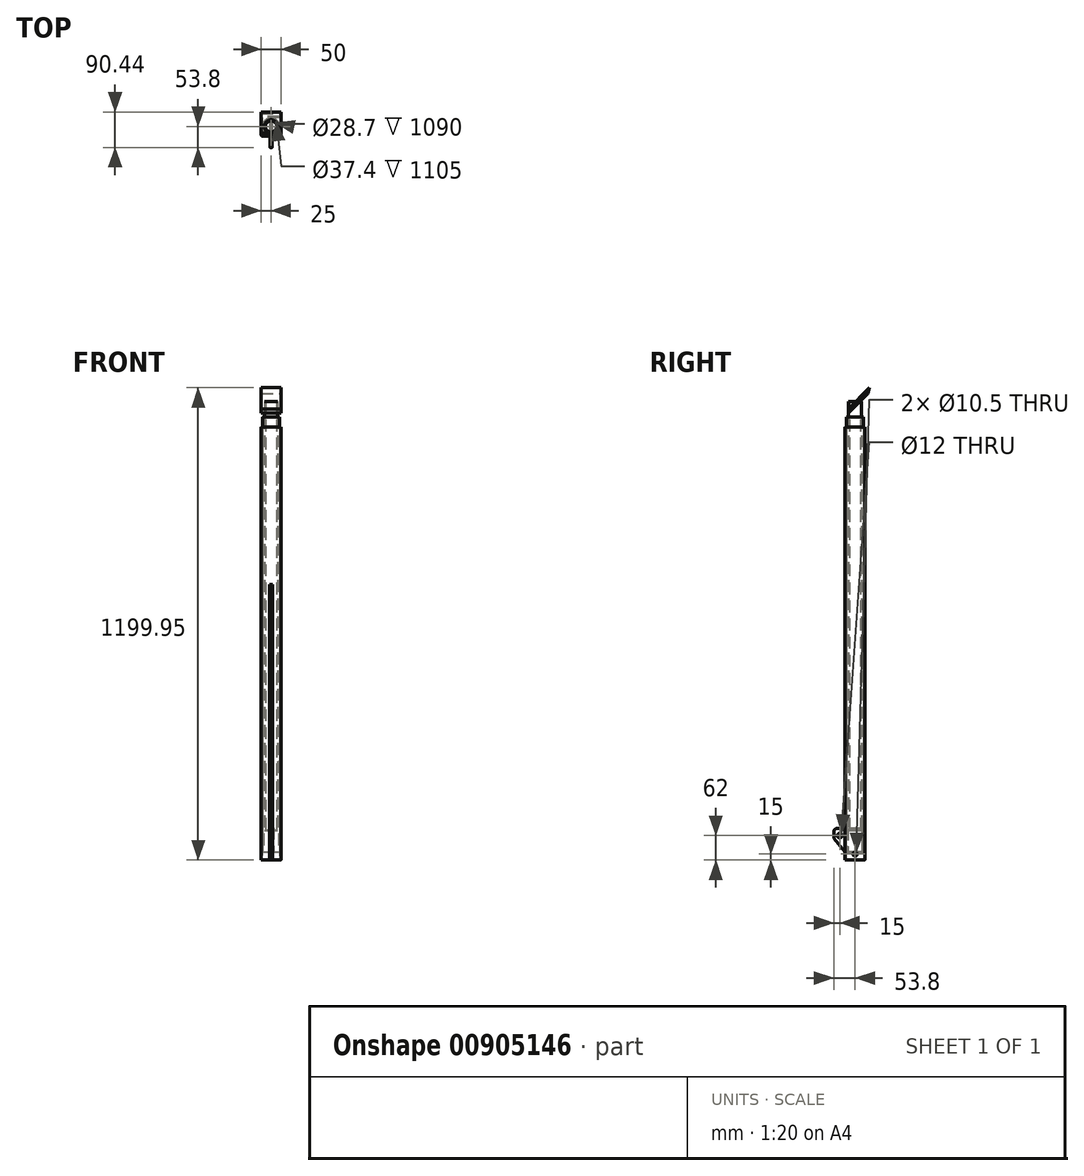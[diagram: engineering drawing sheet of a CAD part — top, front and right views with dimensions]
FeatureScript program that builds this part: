
annotation { "Feature Type Name" : "Feature", "Feature Type Description" : "" }
export const myFeature = defineFeature(function(context is Context, id is Id, definition is map)
    precondition{}
    {
        {
            var Q0;
            Q0=qCreatedBy(makeId("Top.planeOp"),FACE);
            var sketch = newSketch(context, id + "F0", { "sketchPlane" : qUnion([Q0])});
            skLineSegment(sketch, "E0.bottom", {"start": v(21, 25) * mm, "end": v(-21, 25) * mm});
            skLineSegment(sketch, "E0.top", {"start": v(21, -25) * mm, "end": v(-21, -25) * mm});
            skLineSegment(sketch, "E0.left", {"start": v(25, 21) * mm, "end": v(25, -21) * mm});
            skLineSegment(sketch, "E0.right", {"start": v(-25, 21) * mm, "end": v(-25, -21) * mm});
            skPoint(sketch, "E0.middle", {"position": v(0, 0) * mm});
            skLineSegment(sketch, "E1.bottom", {"start": v(21, 23) * mm, "end": v(-21, 23) * mm});
            skLineSegment(sketch, "E1.top", {"start": v(21, -23) * mm, "end": v(-21, -23) * mm});
            skLineSegment(sketch, "E1.left", {"start": v(23, 21) * mm, "end": v(23, -21) * mm});
            skLineSegment(sketch, "E1.right", {"start": v(-23, 21) * mm, "end": v(-23, -21) * mm});
            skPoint(sketch, "E2.visualSharp", {"position": v(-25, 25) * mm});
            skArc(sketch, "E2.filletArc", {"start": v(-21, 25) * mm, "mid": v(-23.83, 23.83) * mm, "end": v(-25, 21) * mm});
            skPoint(sketch, "E3.visualSharp", {"position": v(25, 25) * mm});
            skArc(sketch, "E3.filletArc", {"start": v(25, 21) * mm, "mid": v(23.83, 23.83) * mm, "end": v(21, 25) * mm});
            skPoint(sketch, "E4.visualSharp", {"position": v(25, -25) * mm});
            skArc(sketch, "E4.filletArc", {"start": v(21, -25) * mm, "mid": v(23.83, -23.83) * mm, "end": v(25, -21) * mm});
            skPoint(sketch, "E5.visualSharp", {"position": v(-25, -25) * mm});
            skArc(sketch, "E5.filletArc", {"start": v(-25, -21) * mm, "mid": v(-23.83, -23.83) * mm, "end": v(-21, -25) * mm});
            skPoint(sketch, "E6.visualSharp", {"position": v(23, 23) * mm});
            skArc(sketch, "E6.filletArc", {"start": v(23, 21) * mm, "mid": v(22.41, 22.41) * mm, "end": v(21, 23) * mm});
            skPoint(sketch, "E7.visualSharp", {"position": v(23, -23) * mm});
            skArc(sketch, "E7.filletArc", {"start": v(21, -23) * mm, "mid": v(22.41, -22.41) * mm, "end": v(23, -21) * mm});
            skPoint(sketch, "E8.visualSharp", {"position": v(-23, -23) * mm});
            skArc(sketch, "E8.filletArc", {"start": v(-23, -21) * mm, "mid": v(-22.41, -22.41) * mm, "end": v(-21, -23) * mm});
            skPoint(sketch, "E9.visualSharp", {"position": v(-23, 23) * mm});
            skArc(sketch, "E9.filletArc", {"start": v(-21, 23) * mm, "mid": v(-22.41, 22.41) * mm, "end": v(-23, 21) * mm});
            skSolve(sketch);
        }
        {
            var Q0;
            Q0=makeQuery(id+"F0.imprint","IMPRINT",FACE,{"disambiguationData":[TD([[makeQuery(id+"F0.imprint","IMPRINT",EDGE,{"derivedFrom":sQuery(id+"F0.wireOp",EDGE,"E0.bottom")}),1.0]])]});
            extrude(context, id + "F1", {"entities" : qUnion([Q0]), "depth" : 1100 * mm, "offsetDistance" : 25 * mm});
        }
        {
            var Q0;
            Q0=qCreatedBy(makeId("Top.planeOp"),FACE);
            var sketch = newSketch(context, id + "F2", { "sketchPlane" : qUnion([Q0])});
            skCircle(sketch, "E10", {"center": v(0, 0) * mm, "radius": 21.2 * mm});
            skCircle(sketch, "E11", {"center": v(0, 0) * mm, "radius": 18.7 * mm});
            skSolve(sketch);
        }
        {
            var Q0;
            Q0=makeQuery(id+"F2.imprint","IMPRINT",FACE,{"disambiguationData":[TD([[makeQuery(id+"F2.imprint","IMPRINT",EDGE,{"derivedFrom":sQuery(id+"F2.wireOp",EDGE,"E10")}),1.0]])]});
            extrude(context, id + "F3", {"entities" : qUnion([Q0]), "depth" : 1105 * mm, "offsetDistance" : 25 * mm});
        }
        {
            var Q0;
            Q0=qCreatedBy(makeId("Top.planeOp"),FACE);
            var sketch = newSketch(context, id + "F4", { "sketchPlane" : qUnion([Q0])});
            skCircle(sketch, "E12", {"center": v(0, 0) * mm, "radius": 16.85 * mm});
            skCircle(sketch, "E13", {"center": v(0, 0) * mm, "radius": 14.35 * mm});
            skSolve(sketch);
        }
        {
            var Q0;
            Q0=makeQuery(id+"F4.imprint","IMPRINT",FACE,{"disambiguationData":[TD([[makeQuery(id+"F4.imprint","IMPRINT",EDGE,{"derivedFrom":sQuery(id+"F4.wireOp",EDGE,"E12")}),1.0]])]});
            extrude(context, id + "F5", {"entities" : qUnion([Q0]), "depth" : 1090 * mm, "offsetDistance" : 25 * mm});
        }
        {
            var Q0;
            Q0=makeQuery(id+"F1.opExtrude","SWEPT_FACE",FACE,{"disambiguationData":[OSD([sQuery(id+"F0.wireOp",EDGE,"E0.top")])]});
            var sketch = newSketch(context, id + "F6", { "sketchPlane" : qUnion([Q0])});
            skLineSegment(sketch, "E14.bottom", {"start": v(-4, 0) * mm, "end": v(4, 0) * mm});
            skLineSegment(sketch, "E14.top", {"start": v(-4, 700) * mm, "end": v(4, 700) * mm});
            skLineSegment(sketch, "E14.left", {"start": v(-4, 0) * mm, "end": v(-4, 700) * mm});
            skLineSegment(sketch, "E14.right", {"start": v(4, 0) * mm, "end": v(4, 700) * mm});
            skSolve(sketch);
        }
        {
            var Q0;
            Q0=makeQuery(id+"F6.imprint","IMPRINT",FACE,{"disambiguationData":[TD([[makeQuery(id+"F6.imprint","IMPRINT",EDGE,{"derivedFrom":sQuery(id+"F6.wireOp",EDGE,"E14.bottom")}),-1.0]])]});
            extrude(context, id + "F7", {"entities" : qUnion([Q0]), "operationType" : NewBodyOperationType.REMOVE, "endBound" : BoundingType.UP_TO_NEXT, "oppositeDirection" : true, "depth" : 25 * mm, "offsetDistance" : 25 * mm});
        }
        {
            var Q0;
            Q0=makeQuery(id+"F3.opExtrude","SWEPT_BODY",BODY,{"disambiguationData":[OSD([sQuery(id+"F2.wireOp",EDGE,"E10"),sQuery(id+"F2.wireOp",EDGE,"E11")])]});
            var Q1;
            Q1=makeQuery(id+"F5.opExtrude","SWEPT_BODY",BODY,{"disambiguationData":[OSD([sQuery(id+"F4.wireOp",EDGE,"E12"),sQuery(id+"F4.wireOp",EDGE,"E13")])]});
            transform(context, id + "F8", {"entities" : qUnion([Q0, Q1]), "transformType" : TransformType.TRANSLATION_3D, "dx" : 0 * mm, "dy" : 0 * mm, "dz" : 25 * mm, "makeCopy" : false});
        }
        {
            var Q0;
            Q0=makeQuery(id+"F3.opExtrude","SWEPT_BODY",BODY,{"disambiguationData":[OSD([sQuery(id+"F2.wireOp",EDGE,"E10"),sQuery(id+"F2.wireOp",EDGE,"E11")])]});
            transform(context, id + "F9", {"entities" : qUnion([Q0]), "transformType" : TransformType.TRANSLATION_3D, "dx" : 0 * mm, "dy" : 0 * mm, "dz" : -25 * mm, "makeCopy" : false});
        }
        {
            var Q0;
            Q0=makeQuery(id+"F1.opExtrude","SWEPT_FACE",FACE,{"disambiguationData":[OSD([sQuery(id+"F0.wireOp",EDGE,"E0.left")])]});
            var sketch = newSketch(context, id + "F10", { "sketchPlane" : qUnion([Q0])});
            skCircle(sketch, "E15", {"center": v(0, 15) * mm, "radius": 5.25 * mm});
            skSolve(sketch);
        }
        {
            var Q0;
            Q0=makeQuery(id+"F5.opExtrude","SWEPT_BODY",BODY,{"disambiguationData":[OSD([sQuery(id+"F4.wireOp",EDGE,"E12"),sQuery(id+"F4.wireOp",EDGE,"E13")])]});
            transform(context, id + "F11", {"entities" : qUnion([Q0]), "transformType" : TransformType.TRANSLATION_3D, "dx" : 0 * mm, "dy" : 0 * mm, "dz" : 50 * mm, "makeCopy" : false});
        }
        {
            var Q0;
            Q0=qCreatedBy(makeId("Right.planeOp"),FACE);
            var sketch = newSketch(context, id + "F12", { "sketchPlane" : qUnion([Q0])});
            skLineSegment(sketch, "E16", {"start": v(21.2, 0) * mm, "end": v(21.2, 60) * mm});
            skLineSegment(sketch, "E17", {"start": v(21.2, 60) * mm, "end": v(-53.8, 60) * mm});
            skLineSegment(sketch, "E18", {"start": v(-53.8, 60) * mm, "end": v(-53.8, 35) * mm});
            skLineSegment(sketch, "E19", {"start": v(-53.8, 35) * mm, "end": v(-25, 0) * mm});
            skLineSegment(sketch, "E20", {"start": v(-25, 0) * mm, "end": v(21.2, 0) * mm});
            skSolve(sketch);
        }
        {
            var Q0;
            Q0=makeQuery(id+"F12.imprint","IMPRINT",FACE,{"disambiguationData":[TD([[makeQuery(id+"F12.imprint","IMPRINT",EDGE,{"derivedFrom":sQuery(id+"F12.wireOp",EDGE,"E16")}),1.0]])]});
            extrude(context, id + "F13", {"entities" : qUnion([Q0]), "operationType" : NewBodyOperationType.REMOVE, "depth" : 4 * mm, "offsetDistance" : 25 * mm, "hasSecondDirection" : true, "secondDirectionOppositeDirection" : true, "secondDirectionDepth" : 4 * mm});
        }
        {
            var Q0;
            Q0=makeQuery(id+"F13.boolean.opBoolean","INTERSECT",EDGE,{"disambiguationData":[OD(0.0)],"derivedFrom":[makeQuery(id+"F3.opExtrude","SWEPT_FACE",FACE,{"disambiguationData":[OSD([sQuery(id+"F2.wireOp",EDGE,"E10")])]}),makeQuery(id+"F13.opExtrude","CAP_FACE",FACE,{"disambiguationData":[OSD([sQuery(id+"F12.wireOp",EDGE,"E16"),sQuery(id+"F12.wireOp",EDGE,"E17"),sQuery(id+"F12.wireOp",EDGE,"E18"),sQuery(id+"F12.wireOp",EDGE,"E19"),sQuery(id+"F12.wireOp",EDGE,"E20")])],"isStart":true})]});
            var Q1;
            Q1=makeQuery(id+"F13.boolean.opBoolean","INTERSECT",EDGE,{"disambiguationData":[OD(0.0)],"derivedFrom":[makeQuery(id+"F3.opExtrude","SWEPT_FACE",FACE,{"disambiguationData":[OSD([sQuery(id+"F2.wireOp",EDGE,"E10")])]}),makeQuery(id+"F13.opExtrude","CAP_FACE",FACE,{"disambiguationData":[OSD([sQuery(id+"F12.wireOp",EDGE,"E16"),sQuery(id+"F12.wireOp",EDGE,"E17"),sQuery(id+"F12.wireOp",EDGE,"E18"),sQuery(id+"F12.wireOp",EDGE,"E19"),sQuery(id+"F12.wireOp",EDGE,"E20")])],"isStart":false})]});
            var Q2;
            Q2=makeQuery(id+"F13.boolean.opBoolean","INTERSECT",EDGE,{"disambiguationData":[OD(0.0)],"derivedFrom":[makeQuery(id+"F3.opExtrude","SWEPT_FACE",FACE,{"disambiguationData":[OSD([sQuery(id+"F2.wireOp",EDGE,"E10")])]}),makeQuery(id+"F13.opExtrude","SWEPT_FACE",FACE,{"disambiguationData":[OSD([sQuery(id+"F12.wireOp",EDGE,"E17")])]})]});
            var Q3;
            Q3=makeQuery(id+"F13.boolean.opBoolean","INTERSECT",EDGE,{"disambiguationData":[OD(1.0)],"derivedFrom":[makeQuery(id+"F3.opExtrude","SWEPT_FACE",FACE,{"disambiguationData":[OSD([sQuery(id+"F2.wireOp",EDGE,"E10")])]}),makeQuery(id+"F13.opExtrude","CAP_FACE",FACE,{"disambiguationData":[OSD([sQuery(id+"F12.wireOp",EDGE,"E16"),sQuery(id+"F12.wireOp",EDGE,"E17"),sQuery(id+"F12.wireOp",EDGE,"E18"),sQuery(id+"F12.wireOp",EDGE,"E19"),sQuery(id+"F12.wireOp",EDGE,"E20")])],"isStart":false})]});
            var Q4;
            Q4=makeQuery(id+"F13.boolean.opBoolean","INTERSECT",EDGE,{"disambiguationData":[OD(1.0)],"derivedFrom":[makeQuery(id+"F3.opExtrude","SWEPT_FACE",FACE,{"disambiguationData":[OSD([sQuery(id+"F2.wireOp",EDGE,"E10")])]}),makeQuery(id+"F13.opExtrude","CAP_FACE",FACE,{"disambiguationData":[OSD([sQuery(id+"F12.wireOp",EDGE,"E16"),sQuery(id+"F12.wireOp",EDGE,"E17"),sQuery(id+"F12.wireOp",EDGE,"E18"),sQuery(id+"F12.wireOp",EDGE,"E19"),sQuery(id+"F12.wireOp",EDGE,"E20")])],"isStart":true})]});
            var Q5;
            Q5=makeQuery(id+"F13.boolean.opBoolean","INTERSECT",EDGE,{"disambiguationData":[OD(1.0)],"derivedFrom":[makeQuery(id+"F3.opExtrude","SWEPT_FACE",FACE,{"disambiguationData":[OSD([sQuery(id+"F2.wireOp",EDGE,"E10")])]}),makeQuery(id+"F13.opExtrude","SWEPT_FACE",FACE,{"disambiguationData":[OSD([sQuery(id+"F12.wireOp",EDGE,"E17")])]})]});
            chamfer(context, id + "F14", {"entities" : qUnion([Q0, Q1, Q2, Q3, Q4, Q5]), "width" : 2 * mm, "tangentPropagation" : true});
        }
        {
            var Q0;
            Q0 = qSketchRegion(id + "F12", true);
            extrude(context, id + "F15", {"entities" : qUnion([Q0]), "depth" : 3 * mm, "offsetDistance" : 25 * mm, "hasSecondDirection" : true, "secondDirectionOppositeDirection" : true, "secondDirectionDepth" : 3 * mm});
        }
        {
            var Q0;
            Q0=makeQuery(id+"F15.opExtrude","CAP_EDGE",EDGE,{"disambiguationData":[OSD([sQuery(id+"F12.wireOp",EDGE,"E16")])],"isStart":false});
            var Q1;
            Q1=makeQuery(id+"F15.opExtrude","CAP_EDGE",EDGE,{"disambiguationData":[OSD([sQuery(id+"F12.wireOp",EDGE,"E16")])],"isStart":true});
            chamfer(context, id + "F16", {"entities" : qUnion([Q0, Q1]), "width" : 2 * mm, "tangentPropagation" : true});
        }
        {
            var Q0;
            Q0=makeQuery(id+"F15.opExtrude","CAP_FACE",FACE,{"disambiguationData":[OSD([sQuery(id+"F12.wireOp",EDGE,"E16"),sQuery(id+"F12.wireOp",EDGE,"E17"),sQuery(id+"F12.wireOp",EDGE,"E18"),sQuery(id+"F12.wireOp",EDGE,"E19"),sQuery(id+"F12.wireOp",EDGE,"E20")])],"isStart":false});
            var sketch = newSketch(context, id + "F17", { "sketchPlane" : qUnion([Q0])});
            skCircle(sketch, "E21", {"center": v(-38.8, 42) * mm, "radius": 6 * mm});
            skSolve(sketch);
        }
        {
            var Q0;
            Q0 = qSketchRegion(id + "F17", true);
            extrude(context, id + "F18", {"entities" : qUnion([Q0]), "operationType" : NewBodyOperationType.REMOVE, "oppositeDirection" : true, "depth" : 10 * mm, "offsetDistance" : 25 * mm});
        }
        {
            var Q0;
            Q0=makeQuery(id+"F15.opExtrude","SWEPT_EDGE",EDGE,{"disambiguationData":[OSD([sQuery(id+"F12.wireOp",EDGE,"E17"),sQuery(id+"F12.wireOp",EDGE,"E18")])]});
            fillet(context, id + "F19", {"entities" : qUnion([Q0]), "radius" : 8 * mm, "tangentPropagation" : true, "allowEdgeOverflow" : false});
        }
        {
            var Q0;
            Q0=makeQuery(id+"F3.opExtrude","SWEPT_BODY",BODY,{"disambiguationData":[OSD([sQuery(id+"F2.wireOp",EDGE,"E10"),sQuery(id+"F2.wireOp",EDGE,"E11")])]});
            var Q1;
            Q1=makeQuery(id+"F15.opExtrude","SWEPT_BODY",BODY,{"disambiguationData":[OSD([sQuery(id+"F12.wireOp",EDGE,"E16"),sQuery(id+"F12.wireOp",EDGE,"E17"),sQuery(id+"F12.wireOp",EDGE,"E18"),sQuery(id+"F12.wireOp",EDGE,"E19"),sQuery(id+"F12.wireOp",EDGE,"E20")])]});
            transform(context, id + "F20", {"entities" : qUnion([Q0, Q1]), "transformType" : TransformType.TRANSLATION_3D, "dx" : 0 * mm, "dy" : 0 * mm, "dz" : 20 * mm, "makeCopy" : false});
        }
        {
            var Q0;
            Q0 = qSketchRegion(id + "F10", true);
            extrude(context, id + "F21", {"entities" : qUnion([Q0]), "operationType" : NewBodyOperationType.REMOVE, "oppositeDirection" : true, "depth" : 50 * mm, "offsetDistance" : 25 * mm});
        }
        {
            var Q0;
            Q0=makeQuery(id+"F1.opExtrude","SWEPT_FACE",FACE,{"disambiguationData":[OSD([sQuery(id+"F0.wireOp",EDGE,"E0.left")])]});
            var sketch = newSketch(context, id + "F22", { "sketchPlane" : qUnion([Q0])});
            skLineSegment(sketch, "E22", {"start": v(32.5, 1184.5) * mm, "end": v(-17, 1135) * mm});
            skLineSegment(sketch, "E23", {"start": v(-17, 1135) * mm, "end": v(-17, 1146.31) * mm});
            skLineSegment(sketch, "E24", {"start": v(-17, 1146.31) * mm, "end": v(36.64, 1199.95) * mm});
            skLineSegment(sketch, "E25", {"start": v(32.5, 1184.5) * mm, "end": v(36.64, 1199.95) * mm});
            skSolve(sketch);
        }
        {
            var Q0;
            Q0=makeQuery(id+"F22.imprint","IMPRINT",FACE,{"disambiguationData":[TD([[makeQuery(id+"F22.imprint","IMPRINT",EDGE,{"derivedFrom":sQuery(id+"F22.wireOp",EDGE,"E22")}),-1.0]])]});
            extrude(context, id + "F23", {"entities" : qUnion([Q0]), "oppositeDirection" : true, "depth" : 50 * mm, "offsetDistance" : 25 * mm});
        }
    });
